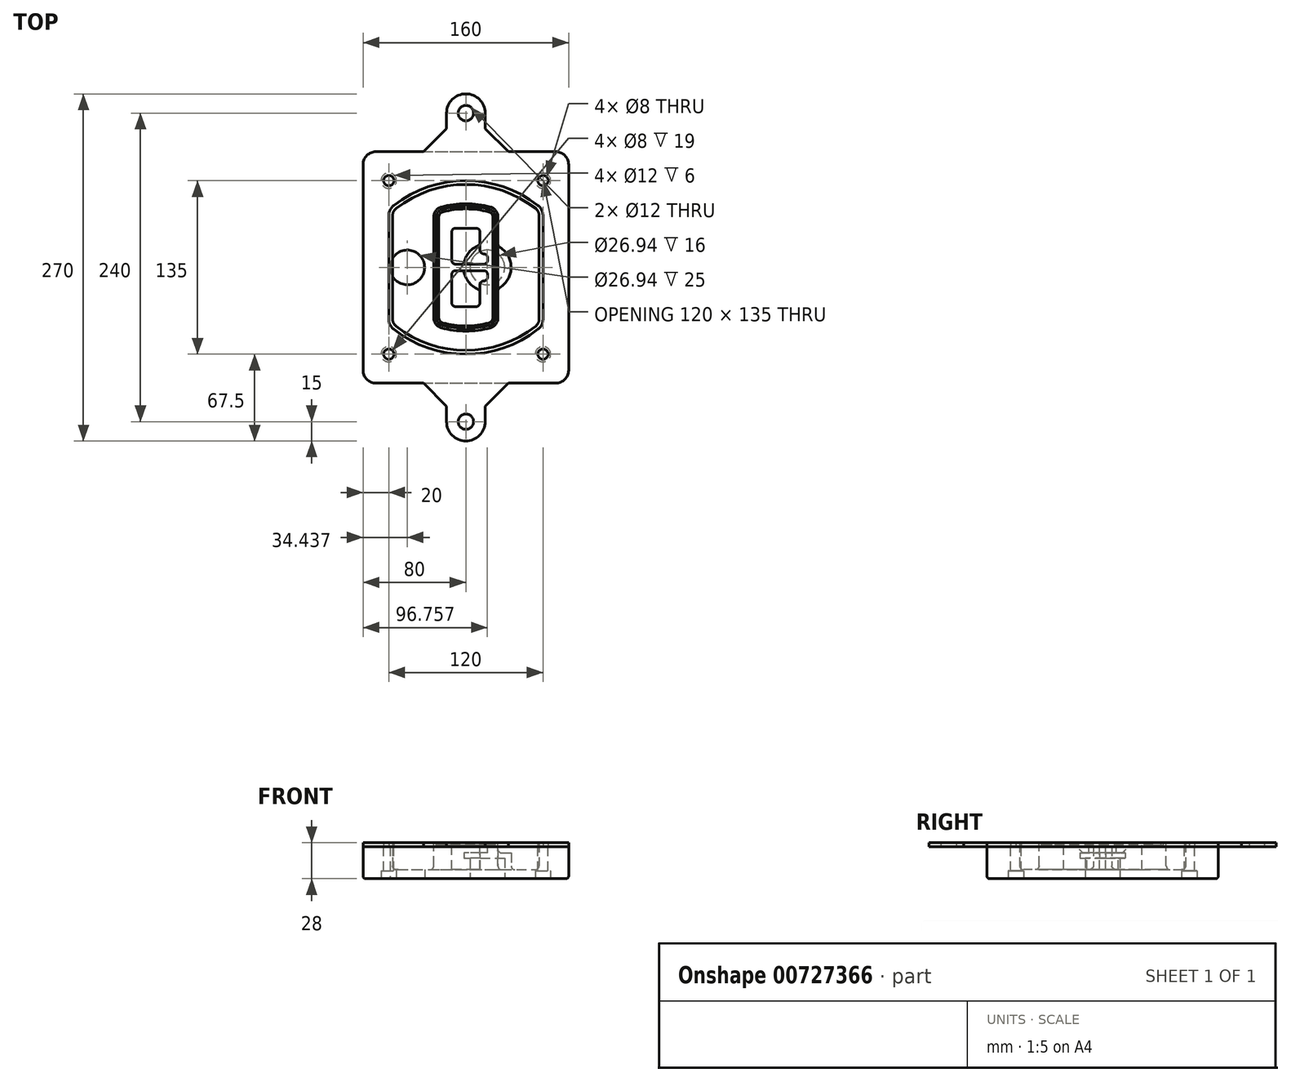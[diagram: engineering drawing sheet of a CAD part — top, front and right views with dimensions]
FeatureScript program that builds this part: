
annotation { "Feature Type Name" : "Feature", "Feature Type Description" : "" }
export const myFeature = defineFeature(function(context is Context, id is Id, definition is map)
    precondition{}
    {
        {
            var Q0;
            Q0=qCreatedBy(makeId("Top.planeOp"),FACE);
            var sketch = newSketch(context, id + "F0", { "sketchPlane" : qUnion([Q0])});
            skPoint(sketch, "E0.rect.middle", {"position": v(0, 0) * mm});
            skLineSegment(sketch, "E1.bottom", {"start": v(-70, -90) * mm, "end": v(70, -90) * mm});
            skLineSegment(sketch, "E1.top", {"start": v(-70, 90) * mm, "end": v(70, 90) * mm});
            skLineSegment(sketch, "E1.left", {"start": v(-80, -80) * mm, "end": v(-80, 80) * mm});
            skLineSegment(sketch, "E1.right", {"start": v(80, -80) * mm, "end": v(80, 80) * mm});
            skLineSegment(sketch, "E2", {"start": v(-80, 90) * mm, "end": v(80, -90) * mm, "construction": true});
            skLineSegment(sketch, "E3", {"start": v(80, 90) * mm, "end": v(-80, -90) * mm, "construction": true});
            skCircle(sketch, "E4", {"center": v(-60, 67.5) * mm, "radius": 4 * mm});
            skCircle(sketch, "E5", {"center": v(60, 67.5) * mm, "radius": 4 * mm});
            skCircle(sketch, "E6", {"center": v(60, -67.5) * mm, "radius": 4 * mm});
            skCircle(sketch, "E7", {"center": v(-60, -67.5) * mm, "radius": 4 * mm});
            skLineSegment(sketch, "E8", {"start": v(-60, 67.5) * mm, "end": v(60, 67.5) * mm, "construction": true});
            skLineSegment(sketch, "E9", {"start": v(60, 67.5) * mm, "end": v(60, -67.5) * mm, "construction": true});
            skLineSegment(sketch, "E10", {"start": v(60, -67.5) * mm, "end": v(-60, -67.5) * mm, "construction": true});
            skLineSegment(sketch, "E11", {"start": v(-60, -67.5) * mm, "end": v(-60, 67.5) * mm, "construction": true});
            skLineSegment(sketch, "E12", {"start": v(-60, 40.3) * mm, "end": v(-60, -40.3) * mm});
            skLineSegment(sketch, "E13", {"start": v(60, 40.3) * mm, "end": v(60, -40.3) * mm});
            skArc(sketch, "E14", {"start": v(56.15, 48.18) * mm, "mid": v(0, 67.5) * mm, "end": v(-56.15, 48.18) * mm});
            skArc(sketch, "E15", {"start": v(-56.15, -48.18) * mm, "mid": v(0, -67.5) * mm, "end": v(56.15, -48.18) * mm});
            skLineSegment(sketch, "E16", {"start": v(-60, 0) * mm, "end": v(60, 0) * mm, "construction": true});
            skPoint(sketch, "E17.visualSharp", {"position": v(-60, -45) * mm});
            skArc(sketch, "E17.filletArc", {"start": v(-60, -40.3) * mm, "mid": v(-58.99, -44.68) * mm, "end": v(-56.15, -48.18) * mm});
            skPoint(sketch, "E18.visualSharp", {"position": v(-60, 45) * mm});
            skArc(sketch, "E18.filletArc", {"start": v(-56.15, 48.18) * mm, "mid": v(-58.99, 44.68) * mm, "end": v(-60, 40.3) * mm});
            skPoint(sketch, "E19.visualSharp", {"position": v(60, 45) * mm});
            skArc(sketch, "E19.filletArc", {"start": v(60, 40.3) * mm, "mid": v(58.99, 44.68) * mm, "end": v(56.15, 48.18) * mm});
            skPoint(sketch, "E20.visualSharp", {"position": v(60, -45) * mm});
            skArc(sketch, "E20.filletArc", {"start": v(56.15, -48.18) * mm, "mid": v(58.99, -44.68) * mm, "end": v(60, -40.3) * mm});
            skPoint(sketch, "E21.visualSharp", {"position": v(-80, 90) * mm});
            skArc(sketch, "E21.filletArc", {"start": v(-70, 90) * mm, "mid": v(-77.07, 87.07) * mm, "end": v(-80, 80) * mm});
            skPoint(sketch, "E22.visualSharp", {"position": v(80, 90) * mm});
            skArc(sketch, "E22.filletArc", {"start": v(80, 80) * mm, "mid": v(77.07, 87.07) * mm, "end": v(70, 90) * mm});
            skPoint(sketch, "E23.visualSharp", {"position": v(80, -90) * mm});
            skArc(sketch, "E23.filletArc", {"start": v(70, -90) * mm, "mid": v(77.07, -87.07) * mm, "end": v(80, -80) * mm});
            skPoint(sketch, "E24.visualSharp", {"position": v(-80, -90) * mm});
            skArc(sketch, "E24.filletArc", {"start": v(-80, -80) * mm, "mid": v(-77.07, -87.07) * mm, "end": v(-70, -90) * mm});
            skArc(sketch, "E25.0", {"start": v(57, 40.3) * mm, "mid": v(56.3, 43.36) * mm, "end": v(54.3, 45.81) * mm});
            skLineSegment(sketch, "E25.1", {"start": v(57, 40.3) * mm, "end": v(57, -40.3) * mm});
            skArc(sketch, "E25.2", {"start": v(54.3, -45.81) * mm, "mid": v(56.3, -43.36) * mm, "end": v(57, -40.3) * mm});
            skArc(sketch, "E25.3", {"start": v(-54.3, -45.81) * mm, "mid": v(0, -64.5) * mm, "end": v(54.3, -45.81) * mm});
            skArc(sketch, "E25.4", {"start": v(-57, -40.3) * mm, "mid": v(-56.3, -43.36) * mm, "end": v(-54.3, -45.81) * mm});
            skArc(sketch, "E25.5", {"start": v(54.3, 45.81) * mm, "mid": v(0, 64.5) * mm, "end": v(-54.3, 45.81) * mm});
            skLineSegment(sketch, "E25.6", {"start": v(-57, 40.3) * mm, "end": v(-57, -40.3) * mm});
            skArc(sketch, "E25.7", {"start": v(-54.3, 45.81) * mm, "mid": v(-56.3, 43.36) * mm, "end": v(-57, 40.3) * mm});
            skArc(sketch, "E26.0", {"start": v(-58.62, 51.33) * mm, "mid": v(-62.58, 46.43) * mm, "end": v(-64, 40.3) * mm});
            skArc(sketch, "E26.1", {"start": v(58.62, 51.33) * mm, "mid": v(0, 71.5) * mm, "end": v(-58.62, 51.33) * mm});
            skArc(sketch, "E26.2", {"start": v(64, 40.3) * mm, "mid": v(62.58, 46.43) * mm, "end": v(58.62, 51.33) * mm});
            skLineSegment(sketch, "E26.3", {"start": v(64, 40.3) * mm, "end": v(64, -40.3) * mm});
            skArc(sketch, "E26.4", {"start": v(58.62, -51.33) * mm, "mid": v(62.58, -46.43) * mm, "end": v(64, -40.3) * mm});
            skLineSegment(sketch, "E26.5", {"start": v(-64, 40.3) * mm, "end": v(-64, -40.3) * mm});
            skArc(sketch, "E26.6", {"start": v(-58.62, -51.33) * mm, "mid": v(0, -71.5) * mm, "end": v(58.62, -51.33) * mm});
            skArc(sketch, "E26.7", {"start": v(-64, -40.3) * mm, "mid": v(-62.58, -46.43) * mm, "end": v(-58.62, -51.33) * mm});
            skSolve(sketch);
        }
        {
            var Q0;
            Q0=makeQuery(id+"F0.imprint","IMPRINT",FACE,{"disambiguationData":[TD([[makeQuery(id+"F0.imprint","IMPRINT",EDGE,{"derivedFrom":sQuery(id+"F0.wireOp",EDGE,"E1.bottom")}),1.0]])]});
            var Q1;
            Q1=makeQuery(id+"F0.imprint","IMPRINT",FACE,{"disambiguationData":[TD([[makeQuery(id+"F0.imprint","IMPRINT",EDGE,{"derivedFrom":sQuery(id+"F0.wireOp",EDGE,"E12")}),1.0]])]});
            var Q2;
            Q2=makeQuery(id+"F0.imprint","IMPRINT",FACE,{"disambiguationData":[TD([[makeQuery(id+"F0.imprint","IMPRINT",EDGE,{"derivedFrom":sQuery(id+"F0.wireOp",EDGE,"E25.0")}),1.0]])]});
            var Q3;
            Q3=makeQuery(id+"F0.imprint","IMPRINT",FACE,{"disambiguationData":[TD([[makeQuery(id+"F0.imprint","IMPRINT",EDGE,{"derivedFrom":sQuery(id+"F0.wireOp",EDGE,"E12")}),-1.0]])]});
            extrude(context, id + "F1", {"entities" : qUnion([Q0, Q1, Q2, Q3]), "oppositeDirection" : true, "depth" : 25 * mm});
        }
        {
            var Q0;
            Q0=makeQuery(id+"F0.imprint","IMPRINT",FACE,{"disambiguationData":[TD([[makeQuery(id+"F0.imprint","IMPRINT",EDGE,{"derivedFrom":sQuery(id+"F0.wireOp",EDGE,"E12")}),1.0]])]});
            extrude(context, id + "F2", {"entities" : qUnion([Q0]), "operationType" : NewBodyOperationType.ADD, "depth" : 3 * mm});
        }
        {
            var Q0;
            Q0=makeQuery(id+"F0.imprint","IMPRINT",FACE,{"disambiguationData":[TD([[makeQuery(id+"F0.imprint","IMPRINT",EDGE,{"derivedFrom":sQuery(id+"F0.wireOp",EDGE,"E25.0")}),1.0]])]});
            extrude(context, id + "F3", {"entities" : qUnion([Q0]), "operationType" : NewBodyOperationType.REMOVE, "oppositeDirection" : true, "depth" : 18 * mm});
        }
        {
            var Q0;
            Q0=makeQuery(id+"F2.opExtrude","CAP_FACE",FACE,{"disambiguationData":[OSD([sQuery(id+"F0.wireOp",EDGE,"E12"),sQuery(id+"F0.wireOp",EDGE,"E13"),sQuery(id+"F0.wireOp",EDGE,"E14"),sQuery(id+"F0.wireOp",EDGE,"E15"),sQuery(id+"F0.wireOp",EDGE,"E17.filletArc"),sQuery(id+"F0.wireOp",EDGE,"E18.filletArc"),sQuery(id+"F0.wireOp",EDGE,"E19.filletArc"),sQuery(id+"F0.wireOp",EDGE,"E20.filletArc"),sQuery(id+"F0.wireOp",EDGE,"E25.0"),sQuery(id+"F0.wireOp",EDGE,"E25.1"),sQuery(id+"F0.wireOp",EDGE,"E25.2"),sQuery(id+"F0.wireOp",EDGE,"E25.3"),sQuery(id+"F0.wireOp",EDGE,"E25.4"),sQuery(id+"F0.wireOp",EDGE,"E25.5"),sQuery(id+"F0.wireOp",EDGE,"E25.6"),sQuery(id+"F0.wireOp",EDGE,"E25.7")])],"isStart":false});
            var sketch = newSketch(context, id + "F4", { "sketchPlane" : qUnion([Q0])});
            skArc(sketch, "E27.0", {"start": v(-19.08, -46.97) * mm, "mid": v(0, -49.5) * mm, "end": v(19.08, -46.97) * mm});
            skArc(sketch, "E28.0", {"start": v(19.08, 46.97) * mm, "mid": v(0, 49.5) * mm, "end": v(-19.08, 46.97) * mm});
            skLineSegment(sketch, "E29", {"start": v(-25, 39.25) * mm, "end": v(-25, -39.25) * mm});
            skLineSegment(sketch, "E30", {"start": v(25, 39.25) * mm, "end": v(25, -39.25) * mm});
            skLineSegment(sketch, "E31", {"start": v(-25, 45.1) * mm, "end": v(25, 45.1) * mm, "construction": true});
            skLineSegment(sketch, "E32", {"start": v(-25, -45.1) * mm, "end": v(25, -45.1) * mm, "construction": true});
            skPoint(sketch, "E33.visualSharp", {"position": v(-25, 45.1) * mm});
            skArc(sketch, "E33.filletArc", {"start": v(-19.08, 46.97) * mm, "mid": v(-23.35, 44.11) * mm, "end": v(-25, 39.25) * mm});
            skPoint(sketch, "E34.visualSharp", {"position": v(25, 45.1) * mm});
            skArc(sketch, "E34.filletArc", {"start": v(25, 39.25) * mm, "mid": v(23.35, 44.11) * mm, "end": v(19.08, 46.97) * mm});
            skPoint(sketch, "E35.visualSharp", {"position": v(25, -45.1) * mm});
            skArc(sketch, "E35.filletArc", {"start": v(19.08, -46.97) * mm, "mid": v(23.35, -44.11) * mm, "end": v(25, -39.25) * mm});
            skPoint(sketch, "E36.visualSharp", {"position": v(-25, -45.1) * mm});
            skArc(sketch, "E36.filletArc", {"start": v(-25, -39.25) * mm, "mid": v(-23.35, -44.11) * mm, "end": v(-19.08, -46.97) * mm});
            skArc(sketch, "E37.0", {"start": v(54.3, 45.81) * mm, "mid": v(0, 64.5) * mm, "end": v(-54.3, 45.81) * mm});
            skArc(sketch, "E37.1", {"start": v(-54.3, 45.81) * mm, "mid": v(-56.3, 43.36) * mm, "end": v(-57, 40.3) * mm});
            skLineSegment(sketch, "E37.2", {"start": v(-57, 40.3) * mm, "end": v(-57, -40.3) * mm});
            skArc(sketch, "E37.3", {"start": v(-57, -40.3) * mm, "mid": v(-56.3, -43.36) * mm, "end": v(-54.3, -45.81) * mm});
            skArc(sketch, "E37.4", {"start": v(-54.3, -45.81) * mm, "mid": v(0, -64.5) * mm, "end": v(54.3, -45.81) * mm});
            skArc(sketch, "E37.5", {"start": v(54.3, -45.81) * mm, "mid": v(56.3, -43.36) * mm, "end": v(57, -40.3) * mm});
            skLineSegment(sketch, "E37.6", {"start": v(57, 40.3) * mm, "end": v(57, -40.3) * mm});
            skArc(sketch, "E37.7", {"start": v(57, 40.3) * mm, "mid": v(56.3, 43.36) * mm, "end": v(54.3, 45.81) * mm});
            skLineSegment(sketch, "E38.0", {"start": v(23, 39.25) * mm, "end": v(23, -39.25) * mm});
            skArc(sketch, "E38.1", {"start": v(18.56, -45.04) * mm, "mid": v(21.76, -42.9) * mm, "end": v(23, -39.25) * mm});
            skArc(sketch, "E38.2", {"start": v(-18.56, -45.04) * mm, "mid": v(0, -47.5) * mm, "end": v(18.56, -45.04) * mm});
            skArc(sketch, "E38.3", {"start": v(-23, -39.25) * mm, "mid": v(-21.76, -42.9) * mm, "end": v(-18.56, -45.04) * mm});
            skLineSegment(sketch, "E38.4", {"start": v(-23, 39.25) * mm, "end": v(-23, -39.25) * mm});
            skArc(sketch, "E38.5", {"start": v(23, 39.25) * mm, "mid": v(21.76, 42.9) * mm, "end": v(18.56, 45.04) * mm});
            skArc(sketch, "E38.6", {"start": v(-18.56, 45.04) * mm, "mid": v(-21.76, 42.9) * mm, "end": v(-23, 39.25) * mm});
            skArc(sketch, "E38.7", {"start": v(18.56, 45.04) * mm, "mid": v(0, 47.5) * mm, "end": v(-18.56, 45.04) * mm});
            skArc(sketch, "E39.0", {"start": v(21, 39.25) * mm, "mid": v(20.18, 41.68) * mm, "end": v(18.04, 43.1) * mm});
            skLineSegment(sketch, "E39.1", {"start": v(21, 39.25) * mm, "end": v(21, -39.25) * mm});
            skArc(sketch, "E39.2", {"start": v(18.04, -43.1) * mm, "mid": v(20.18, -41.68) * mm, "end": v(21, -39.25) * mm});
            skArc(sketch, "E39.3", {"start": v(-18.04, -43.1) * mm, "mid": v(0, -45.5) * mm, "end": v(18.04, -43.1) * mm});
            skArc(sketch, "E39.4", {"start": v(-21, -39.25) * mm, "mid": v(-20.18, -41.68) * mm, "end": v(-18.04, -43.1) * mm});
            skArc(sketch, "E39.5", {"start": v(18.04, 43.1) * mm, "mid": v(0, 45.5) * mm, "end": v(-18.04, 43.1) * mm});
            skLineSegment(sketch, "E39.6", {"start": v(-21, 39.25) * mm, "end": v(-21, -39.25) * mm});
            skArc(sketch, "E39.7", {"start": v(-18.04, 43.1) * mm, "mid": v(-20.18, 41.68) * mm, "end": v(-21, 39.25) * mm});
            skLineSegment(sketch, "E40", {"start": v(-25, 0) * mm, "end": v(25, 0) * mm, "construction": true});
            skLineSegment(sketch, "E41", {"start": v(-11, 5.5) * mm, "end": v(-11, 27.5) * mm});
            skLineSegment(sketch, "E42", {"start": v(-8, 30.5) * mm, "end": v(8, 30.5) * mm});
            skLineSegment(sketch, "E43", {"start": v(11, 27.5) * mm, "end": v(11, 13.5) * mm});
            skLineSegment(sketch, "E44", {"start": v(14, 10.5) * mm, "end": v(14, 10.5) * mm});
            skLineSegment(sketch, "E45", {"start": v(17, 7.5) * mm, "end": v(17, 5.5) * mm});
            skLineSegment(sketch, "E46", {"start": v(14, 2.5) * mm, "end": v(-8, 2.5) * mm});
            skPoint(sketch, "E47.visualSharp", {"position": v(-11, 30.5) * mm});
            skArc(sketch, "E47.filletArc", {"start": v(-8, 30.5) * mm, "mid": v(-10.12, 29.62) * mm, "end": v(-11, 27.5) * mm});
            skPoint(sketch, "E48.visualSharp", {"position": v(11, 30.5) * mm});
            skArc(sketch, "E48.filletArc", {"start": v(11, 27.5) * mm, "mid": v(10.12, 29.62) * mm, "end": v(8, 30.5) * mm});
            skPoint(sketch, "E49.visualSharp", {"position": v(11, 10.5) * mm});
            skArc(sketch, "E49.filletArc", {"start": v(11, 13.5) * mm, "mid": v(11.88, 11.38) * mm, "end": v(14, 10.5) * mm});
            skPoint(sketch, "E50.visualSharp", {"position": v(17, 10.5) * mm});
            skArc(sketch, "E50.filletArc", {"start": v(17, 7.5) * mm, "mid": v(16.12, 9.62) * mm, "end": v(14, 10.5) * mm});
            skPoint(sketch, "E51.visualSharp", {"position": v(17, 2.5) * mm});
            skArc(sketch, "E51.filletArc", {"start": v(14, 2.5) * mm, "mid": v(16.12, 3.38) * mm, "end": v(17, 5.5) * mm});
            skPoint(sketch, "E52.visualSharp", {"position": v(-11, 2.5) * mm});
            skArc(sketch, "E52.filletArc", {"start": v(-11, 5.5) * mm, "mid": v(-10.12, 3.38) * mm, "end": v(-8, 2.5) * mm});
            skLineSegment(sketch, "E53.0.MirrorCS", {"start": v(14, -2.5) * mm, "end": v(-8, -2.5) * mm});
            skArc(sketch, "E54.0.MirrorCS", {"start": v(-11, -5.5) * mm, "mid": v(-10.12, -3.38) * mm, "end": v(-8, -2.5) * mm});
            skLineSegment(sketch, "E55.0.MirrorCS", {"start": v(-11, -5.5) * mm, "end": v(-11, -27.5) * mm});
            skArc(sketch, "E56.0.MirrorCS", {"start": v(-8, -30.5) * mm, "mid": v(-10.12, -29.62) * mm, "end": v(-11, -27.5) * mm});
            skLineSegment(sketch, "E57.0.MirrorCS", {"start": v(-8, -30.5) * mm, "end": v(8, -30.5) * mm});
            skArc(sketch, "E58.0.MirrorCS", {"start": v(11, -27.5) * mm, "mid": v(10.12, -29.62) * mm, "end": v(8, -30.5) * mm});
            skLineSegment(sketch, "E59.0.MirrorCS", {"start": v(11, -27.5) * mm, "end": v(11, -13.5) * mm});
            skArc(sketch, "E60.0.MirrorCS", {"start": v(11, -13.5) * mm, "mid": v(11.88, -11.38) * mm, "end": v(14, -10.5) * mm});
            skArc(sketch, "E61.0.MirrorCS", {"start": v(17, -7.5) * mm, "mid": v(16.12, -9.62) * mm, "end": v(14, -10.5) * mm});
            skLineSegment(sketch, "E62.0.MirrorCS", {"start": v(17, -7.5) * mm, "end": v(17, -5.5) * mm});
            skArc(sketch, "E63.0.MirrorCS", {"start": v(14, -2.5) * mm, "mid": v(16.12, -3.38) * mm, "end": v(17, -5.5) * mm});
            skSolve(sketch);
        }
        {
            var Q0;
            Q0=makeQuery(id+"F4.imprint","IMPRINT",FACE,{"disambiguationData":[TD([[makeQuery(id+"F4.imprint","IMPRINT",EDGE,{"derivedFrom":sQuery(id+"F4.wireOp",EDGE,"E27.0")}),1.0]])]});
            var Q1;
            Q1=makeQuery(id+"F4.imprint","IMPRINT",FACE,{"disambiguationData":[TD([[makeQuery(id+"F4.imprint","IMPRINT",EDGE,{"derivedFrom":sQuery(id+"F4.wireOp",EDGE,"E38.0")}),-1.0]])]});
            var Q2;
            Q2=makeQuery(id+"F4.imprint","IMPRINT",FACE,{"disambiguationData":[TD([[makeQuery(id+"F4.imprint","IMPRINT",EDGE,{"derivedFrom":sQuery(id+"F4.wireOp",EDGE,"E39.0")}),1.0]])]});
            extrude(context, id + "F5", {"entities" : qUnion([Q0, Q1, Q2]), "operationType" : NewBodyOperationType.ADD, "endBound" : BoundingType.UP_TO_NEXT, "oppositeDirection" : true, "depth" : 25 * mm});
        }
        {
            var Q0;
            Q0=makeQuery(id+"F4.imprint","IMPRINT",FACE,{"disambiguationData":[TD([[makeQuery(id+"F4.imprint","IMPRINT",EDGE,{"derivedFrom":sQuery(id+"F4.wireOp",EDGE,"E38.0")}),-1.0]])]});
            extrude(context, id + "F6", {"entities" : qUnion([Q0]), "operationType" : NewBodyOperationType.REMOVE, "oppositeDirection" : true, "depth" : 2 * mm});
        }
        {
            var Q0;
            Q0=makeQuery(id+"F1.opExtrude","CAP_FACE",FACE,{"disambiguationData":[OSD([sQuery(id+"F0.wireOp",EDGE,"E1.bottom"),sQuery(id+"F0.wireOp",EDGE,"E1.top"),sQuery(id+"F0.wireOp",EDGE,"E1.left"),sQuery(id+"F0.wireOp",EDGE,"E1.right"),sQuery(id+"F0.wireOp",EDGE,"E4"),sQuery(id+"F0.wireOp",EDGE,"E5"),sQuery(id+"F0.wireOp",EDGE,"E6"),sQuery(id+"F0.wireOp",EDGE,"E7"),sQuery(id+"F0.wireOp",EDGE,"E21.filletArc"),sQuery(id+"F0.wireOp",EDGE,"E22.filletArc"),sQuery(id+"F0.wireOp",EDGE,"E23.filletArc"),sQuery(id+"F0.wireOp",EDGE,"E24.filletArc")])],"isStart":false});
            var sketch = newSketch(context, id + "F7", { "sketchPlane" : qUnion([Q0])});
            skCircle(sketch, "E64", {"center": v(16.76, 0) * mm, "radius": 13.47 * mm});
            skCircle(sketch, "E65", {"center": v(-45.56, 0) * mm, "radius": 13.47 * mm});
            skLineSegment(sketch, "E66", {"start": v(80, 0) * mm, "end": v(-80, 0) * mm});
            skCircle(sketch, "E67", {"center": v(16.76, 0) * mm, "radius": 18.47 * mm});
            skCircle(sketch, "E68", {"center": v(60, -67.5) * mm, "radius": 6 * mm});
            skCircle(sketch, "E69", {"center": v(-60, -67.5) * mm, "radius": 6 * mm});
            skCircle(sketch, "E70", {"center": v(-60, 67.5) * mm, "radius": 6 * mm});
            skCircle(sketch, "E71", {"center": v(60, 67.5) * mm, "radius": 6 * mm});
            skSolve(sketch);
        }
        {
            var Q0;
            {var subQ1=sQuery(id+"F7.wireOp",EDGE,"E66");var subQ4=sQuery(id+"F7.wireOp",EDGE,"E64");var subQ6=makeQuery(id+"F7.imprint","INTERSECT",VERTEX,{"disambiguationData":[OD(0.0)],"derivedFrom":[subQ4,subQ1]});Q0=makeQuery(id+"F7.imprint","IMPRINT",FACE,{"disambiguationData":[TD([[makeQuery(id+"F7.imprint","IMPRINT",EDGE,{"disambiguationData":[TD([[subQ6,-1.0]])],"derivedFrom":subQ4}),-1.0]])]});}
            var Q1;
            {var subQ0=sQuery(id+"F7.wireOp",EDGE,"E66");var subQ1=sQuery(id+"F7.wireOp",EDGE,"E64");var subQ3=makeQuery(id+"F7.imprint","INTERSECT",VERTEX,{"disambiguationData":[OD(0.0)],"derivedFrom":[subQ1,subQ0]});Q1=makeQuery(id+"F7.imprint","IMPRINT",FACE,{"disambiguationData":[TD([[makeQuery(id+"F7.imprint","IMPRINT",EDGE,{"disambiguationData":[TD([[subQ3,-1.0]])],"derivedFrom":subQ1}),1.0]])]});}
            var Q2;
            {var subQ0=sQuery(id+"F7.wireOp",EDGE,"E66");var subQ1=sQuery(id+"F7.wireOp",EDGE,"E64");var subQ3=makeQuery(id+"F7.imprint","INTERSECT",VERTEX,{"disambiguationData":[OD(0.0)],"derivedFrom":[subQ1,subQ0]});Q2=makeQuery(id+"F7.imprint","IMPRINT",FACE,{"disambiguationData":[TD([[makeQuery(id+"F7.imprint","IMPRINT",EDGE,{"disambiguationData":[TD([[subQ3,1.0]])],"derivedFrom":subQ1}),1.0]])]});}
            var Q3;
            {var subQ1=sQuery(id+"F7.wireOp",EDGE,"E66");var subQ4=sQuery(id+"F7.wireOp",EDGE,"E64");var subQ6=makeQuery(id+"F7.imprint","INTERSECT",VERTEX,{"disambiguationData":[OD(0.0)],"derivedFrom":[subQ4,subQ1]});Q3=makeQuery(id+"F7.imprint","IMPRINT",FACE,{"disambiguationData":[TD([[makeQuery(id+"F7.imprint","IMPRINT",EDGE,{"disambiguationData":[TD([[subQ6,1.0]])],"derivedFrom":subQ4}),-1.0]])]});}
            extrude(context, id + "F8", {"entities" : qUnion([Q0, Q1, Q2, Q3]), "operationType" : NewBodyOperationType.ADD, "oppositeDirection" : true, "depth" : 20 * mm});
        }
        {
            var Q0;
            {var subQ0=sQuery(id+"F7.wireOp",EDGE,"E66");var subQ1=sQuery(id+"F7.wireOp",EDGE,"E64");var subQ3=makeQuery(id+"F7.imprint","INTERSECT",VERTEX,{"disambiguationData":[OD(0.0)],"derivedFrom":[subQ1,subQ0]});Q0=makeQuery(id+"F7.imprint","IMPRINT",FACE,{"disambiguationData":[TD([[makeQuery(id+"F7.imprint","IMPRINT",EDGE,{"disambiguationData":[TD([[subQ3,-1.0]])],"derivedFrom":subQ1}),1.0]])]});}
            var Q1;
            {var subQ0=sQuery(id+"F7.wireOp",EDGE,"E66");var subQ1=sQuery(id+"F7.wireOp",EDGE,"E64");var subQ3=makeQuery(id+"F7.imprint","INTERSECT",VERTEX,{"disambiguationData":[OD(0.0)],"derivedFrom":[subQ1,subQ0]});Q1=makeQuery(id+"F7.imprint","IMPRINT",FACE,{"disambiguationData":[TD([[makeQuery(id+"F7.imprint","IMPRINT",EDGE,{"disambiguationData":[TD([[subQ3,1.0]])],"derivedFrom":subQ1}),1.0]])]});}
            extrude(context, id + "F9", {"entities" : qUnion([Q0, Q1]), "operationType" : NewBodyOperationType.REMOVE, "oppositeDirection" : true, "depth" : 16 * mm});
        }
        {
            var Q0;
            {var subQ0=sQuery(id+"F7.wireOp",EDGE,"E66");var subQ1=sQuery(id+"F7.wireOp",EDGE,"E65");var subQ3=makeQuery(id+"F7.imprint","INTERSECT",VERTEX,{"disambiguationData":[OD(0.0)],"derivedFrom":[subQ1,subQ0]});Q0=makeQuery(id+"F7.imprint","IMPRINT",FACE,{"disambiguationData":[TD([[makeQuery(id+"F7.imprint","IMPRINT",EDGE,{"disambiguationData":[TD([[subQ3,-1.0]])],"derivedFrom":subQ1}),1.0]])]});}
            var Q1;
            {var subQ0=sQuery(id+"F7.wireOp",EDGE,"E66");var subQ1=sQuery(id+"F7.wireOp",EDGE,"E65");var subQ3=makeQuery(id+"F7.imprint","INTERSECT",VERTEX,{"disambiguationData":[OD(0.0)],"derivedFrom":[subQ1,subQ0]});Q1=makeQuery(id+"F7.imprint","IMPRINT",FACE,{"disambiguationData":[TD([[makeQuery(id+"F7.imprint","IMPRINT",EDGE,{"disambiguationData":[TD([[subQ3,1.0]])],"derivedFrom":subQ1}),1.0]])]});}
            extrude(context, id + "F10", {"entities" : qUnion([Q0, Q1]), "operationType" : NewBodyOperationType.REMOVE, "oppositeDirection" : true, "depth" : 25 * mm});
        }
        {
            var Q0;
            Q0=makeQuery(id+"F7.imprint","IMPRINT",FACE,{"disambiguationData":[TD([[makeQuery(id+"F7.imprint","IMPRINT",EDGE,{"derivedFrom":sQuery(id+"F7.wireOp",EDGE,"E68")}),1.0]])]});
            var Q1;
            Q1=makeQuery(id+"F7.imprint","IMPRINT",FACE,{"disambiguationData":[TD([[makeQuery(id+"F7.imprint","IMPRINT",EDGE,{"derivedFrom":makeQuery(id+"F1.opExtrude","CAP_EDGE",EDGE,{"disambiguationData":[OSD([sQuery(id+"F0.wireOp",EDGE,"E5")])],"isStart":false})}),-1.0]])]});
            var Q2;
            Q2=makeQuery(id+"F7.imprint","IMPRINT",FACE,{"disambiguationData":[TD([[makeQuery(id+"F7.imprint","IMPRINT",EDGE,{"derivedFrom":sQuery(id+"F7.wireOp",EDGE,"E69")}),1.0]])]});
            var Q3;
            Q3=makeQuery(id+"F7.imprint","IMPRINT",FACE,{"disambiguationData":[TD([[makeQuery(id+"F7.imprint","IMPRINT",EDGE,{"derivedFrom":makeQuery(id+"F1.opExtrude","CAP_EDGE",EDGE,{"disambiguationData":[OSD([sQuery(id+"F0.wireOp",EDGE,"E4")])],"isStart":false})}),-1.0]])]});
            var Q4;
            Q4=makeQuery(id+"F7.imprint","IMPRINT",FACE,{"disambiguationData":[TD([[makeQuery(id+"F7.imprint","IMPRINT",EDGE,{"derivedFrom":sQuery(id+"F7.wireOp",EDGE,"E70")}),1.0]])]});
            var Q5;
            Q5=makeQuery(id+"F7.imprint","IMPRINT",FACE,{"disambiguationData":[TD([[makeQuery(id+"F7.imprint","IMPRINT",EDGE,{"derivedFrom":makeQuery(id+"F1.opExtrude","CAP_EDGE",EDGE,{"disambiguationData":[OSD([sQuery(id+"F0.wireOp",EDGE,"E7")])],"isStart":false})}),-1.0]])]});
            var Q6;
            Q6=makeQuery(id+"F7.imprint","IMPRINT",FACE,{"disambiguationData":[TD([[makeQuery(id+"F7.imprint","IMPRINT",EDGE,{"derivedFrom":sQuery(id+"F7.wireOp",EDGE,"E71")}),1.0]])]});
            var Q7;
            Q7=makeQuery(id+"F7.imprint","IMPRINT",FACE,{"disambiguationData":[TD([[makeQuery(id+"F7.imprint","IMPRINT",EDGE,{"derivedFrom":makeQuery(id+"F1.opExtrude","CAP_EDGE",EDGE,{"disambiguationData":[OSD([sQuery(id+"F0.wireOp",EDGE,"E6")])],"isStart":false})}),-1.0]])]});
            extrude(context, id + "F11", {"entities" : qUnion([Q0, Q1, Q2, Q3, Q4, Q5, Q6, Q7]), "operationType" : NewBodyOperationType.REMOVE, "oppositeDirection" : true, "depth" : 6 * mm});
        }
        {
            var Q0;
            Q0=makeQuery(id+"F9.boolean.opBoolean","COPY",FACE,{"derivedFrom":makeQuery(id+"F9.opExtrude","CAP_FACE",FACE,{"disambiguationData":[OSD([sQuery(id+"F7.wireOp",EDGE,"E64")])],"isStart":false})});
            var sketch = newSketch(context, id + "F12", { "sketchPlane" : qUnion([Q0])});
            skArc(sketch, "E72.0", {"start": v(11, 17.55) * mm, "mid": v(2.57, 11.82) * mm, "end": v(-1.54, 2.5) * mm});
            skArc(sketch, "E72.1", {"start": v(-1.54, -2.5) * mm, "mid": v(2.57, -11.82) * mm, "end": v(11, -17.55) * mm});
            skLineSegment(sketch, "E73", {"start": v(-1.54, -2.5) * mm, "end": v(14, -2.5) * mm});
            skLineSegment(sketch, "E74.0", {"start": v(14, 2.5) * mm, "end": v(-1.54, 2.5) * mm});
            skArc(sketch, "E74.1", {"start": v(14, 2.5) * mm, "mid": v(16.12, 3.38) * mm, "end": v(17, 5.5) * mm});
            skLineSegment(sketch, "E74.2", {"start": v(17, 7.5) * mm, "end": v(17, 5.5) * mm});
            skArc(sketch, "E74.3", {"start": v(17, 7.5) * mm, "mid": v(16.12, 9.62) * mm, "end": v(14, 10.5) * mm});
            skArc(sketch, "E74.4", {"start": v(11, 13.5) * mm, "mid": v(11.88, 11.38) * mm, "end": v(14, 10.5) * mm});
            skLineSegment(sketch, "E74.5", {"start": v(11, 17.55) * mm, "end": v(11, 13.5) * mm});
            skLineSegment(sketch, "E74.7", {"start": v(14, -2.5) * mm, "end": v(-1.54, -2.5) * mm});
            skArc(sketch, "E74.8", {"start": v(14, -2.5) * mm, "mid": v(16.12, -3.38) * mm, "end": v(17, -5.5) * mm});
            skLineSegment(sketch, "E74.9", {"start": v(17, -7.5) * mm, "end": v(17, -5.5) * mm});
            skArc(sketch, "E74.10", {"start": v(17, -7.5) * mm, "mid": v(16.12, -9.62) * mm, "end": v(14, -10.5) * mm});
            skArc(sketch, "E74.11", {"start": v(11, -13.5) * mm, "mid": v(11.88, -11.38) * mm, "end": v(14, -10.5) * mm});
            skLineSegment(sketch, "E74.12", {"start": v(11, -17.55) * mm, "end": v(11, -13.5) * mm});
            skPoint(sketch, "E75.orphan", {"position": v(11, -27.5) * mm});
            skPoint(sketch, "E76.orphan", {"position": v(-8, -2.5) * mm});
            skPoint(sketch, "E77.orphan", {"position": v(-8, 2.5) * mm});
            skPoint(sketch, "E78.orphan", {"position": v(11, 27.5) * mm});
            skSolve(sketch);
        }
        {
            var Q0;
            {var subQ7=sQuery(id+"F12.wireOp",EDGE,"E72.0");var subQ14=sQuery(id+"F12.wireOp",EDGE,"E72.1");var subQ16=sQuery(id+"F12.wireOp",EDGE,"E74.1");var subQ18=sQuery(id+"F12.wireOp",EDGE,"E74.8");Q0=qUnion([makeQuery(id+"F12.imprint","IMPRINT",FACE,{"disambiguationData":[TD([[makeQuery(id+"F12.imprint","IMPRINT",EDGE,{"derivedFrom":subQ7}),1.0]])]}),makeQuery(id+"F12.imprint","IMPRINT",FACE,{"disambiguationData":[TD([[makeQuery(id+"F12.imprint","IMPRINT",EDGE,{"derivedFrom":subQ14}),1.0]])]}),makeQuery(id+"F12.imprint","IMPRINT",FACE,{"disambiguationData":[TD([[makeQuery(id+"F12.imprint","IMPRINT",EDGE,{"derivedFrom":subQ16}),1.0]])]}),makeQuery(id+"F12.imprint","IMPRINT",FACE,{"disambiguationData":[TD([[makeQuery(id+"F12.imprint","IMPRINT",EDGE,{"derivedFrom":subQ18}),-1.0]])]})]);}
            var Q1;
            Q1=makeQuery(id+"F5.boolean.opBoolean","SPLIT",FACE,{"disambiguationData":[TD([makeQuery(id+"F5.opExtrude","SWEPT_FACE",FACE,{"disambiguationData":[OSD([sQuery(id+"F4.wireOp",EDGE,"E41")])]})])],"derivedFrom":makeQuery(id+"F3.boolean.opBoolean","COPY",FACE,{"derivedFrom":makeQuery(id+"F3.opExtrude","CAP_FACE",FACE,{"disambiguationData":[OSD([sQuery(id+"F0.wireOp",EDGE,"E25.0"),sQuery(id+"F0.wireOp",EDGE,"E25.1"),sQuery(id+"F0.wireOp",EDGE,"E25.2"),sQuery(id+"F0.wireOp",EDGE,"E25.3"),sQuery(id+"F0.wireOp",EDGE,"E25.4"),sQuery(id+"F0.wireOp",EDGE,"E25.5"),sQuery(id+"F0.wireOp",EDGE,"E25.6"),sQuery(id+"F0.wireOp",EDGE,"E25.7")])],"isStart":false})})});
            extrude(context, id + "F13", {"entities" : qUnion([Q0]), "operationType" : NewBodyOperationType.REMOVE, "endBound" : BoundingType.UP_TO_SURFACE, "endBoundEntityFace" : qUnion([Q1]), "depth" : 25 * mm});
        }
        {
            var Q0;
            Q0=makeQuery(id+"F3.boolean.opBoolean","COPY",EDGE,{"derivedFrom":makeQuery(id+"F3.opExtrude","CAP_EDGE",EDGE,{"disambiguationData":[OSD([sQuery(id+"F0.wireOp",EDGE,"E25.6")])],"isStart":false})});
            var Q1;
            Q1=makeQuery(id+"F8.boolean.opBoolean","INTERSECT",EDGE,{"derivedFrom":[makeQuery(id+"F5.opExtrude","SWEPT_FACE",FACE,{"disambiguationData":[OSD([sQuery(id+"F4.wireOp",EDGE,"E30")])]}),makeQuery(id+"F8.opExtrude","CAP_FACE",FACE,{"disambiguationData":[OSD([sQuery(id+"F7.wireOp",EDGE,"E67")])],"isStart":false})]});
            var Q2;
            Q2=makeQuery(id+"F8.boolean.opBoolean","INTERSECT",EDGE,{"disambiguationData":[OD(1.0)],"derivedFrom":[makeQuery(id+"F5.opExtrude","SWEPT_FACE",FACE,{"disambiguationData":[OSD([sQuery(id+"F4.wireOp",EDGE,"E30")])]}),makeQuery(id+"F8.opExtrude","SWEPT_FACE",FACE,{"disambiguationData":[OSD([sQuery(id+"F7.wireOp",EDGE,"E67")])]})]});
            var Q3;
            {var subQ0=sQuery(id+"F4.wireOp",EDGE,"E30");Q3=makeQuery(id+"F8.boolean.opBoolean","SPLIT",EDGE,{"disambiguationData":[TD([makeQuery(id+"F5.opExtrude","SWEPT_FACE",FACE,{"disambiguationData":[OSD([sQuery(id+"F4.wireOp",EDGE,"E35.filletArc")])]})])],"derivedFrom":makeQuery(id+"F5.opExtrude","CAP_EDGE",EDGE,{"disambiguationData":[OSD([subQ0])],"isStart":false})});}
            var Q4;
            {var subQ0=sQuery(id+"F0.wireOp",EDGE,"E25.7");var subQ1=sQuery(id+"F0.wireOp",EDGE,"E25.1");var subQ2=sQuery(id+"F0.wireOp",EDGE,"E25.6");var subQ3=sQuery(id+"F0.wireOp",EDGE,"E25.5");var subQ4=sQuery(id+"F0.wireOp",EDGE,"E25.4");var subQ5=sQuery(id+"F0.wireOp",EDGE,"E25.0");var subQ6=sQuery(id+"F0.wireOp",EDGE,"E25.2");var subQ7=sQuery(id+"F0.wireOp",EDGE,"E25.3");Q4=makeQuery(id+"F8.boolean.opBoolean","INTERSECT",EDGE,{"derivedFrom":[makeQuery(id+"F5.boolean.opBoolean","SPLIT",FACE,{"disambiguationData":[TD([makeQuery(id+"F2.opExtrude","SWEPT_FACE",FACE,{"disambiguationData":[OSD([subQ5])]})])],"derivedFrom":makeQuery(id+"F3.boolean.opBoolean","COPY",FACE,{"derivedFrom":makeQuery(id+"F3.opExtrude","CAP_FACE",FACE,{"disambiguationData":[OSD([subQ5,subQ1,subQ6,subQ7,subQ4,subQ3,subQ2,subQ0])],"isStart":false})})}),makeQuery(id+"F8.opExtrude","SWEPT_FACE",FACE,{"disambiguationData":[OSD([sQuery(id+"F7.wireOp",EDGE,"E67")])]})]});}
            var Q5;
            Q5=makeQuery(id+"F8.boolean.opBoolean","INTERSECT",EDGE,{"disambiguationData":[OD(0.0)],"derivedFrom":[makeQuery(id+"F5.opExtrude","SWEPT_FACE",FACE,{"disambiguationData":[OSD([sQuery(id+"F4.wireOp",EDGE,"E30")])]}),makeQuery(id+"F8.opExtrude","SWEPT_FACE",FACE,{"disambiguationData":[OSD([sQuery(id+"F7.wireOp",EDGE,"E67")])]})]});
            fillet(context, id + "F14", {"entities" : qUnion([Q0, Q1, Q2, Q3, Q4, Q5]), "radius" : 3 * mm, "tangentPropagation" : true, "allowEdgeOverflow" : false});
        }
        {
            var Q0;
            Q0=makeQuery(id+"F1.opExtrude","CAP_EDGE",EDGE,{"disambiguationData":[OSD([sQuery(id+"F0.wireOp",EDGE,"E1.bottom")])],"isStart":false});
            fillet(context, id + "F15", {"entities" : qUnion([Q0]), "radius" : 2 * mm, "tangentPropagation" : true, "allowEdgeOverflow" : false});
        }
        {
            var Q0;
            {var subQ0=sQuery(id+"F0.wireOp",EDGE,"E21.filletArc");var subQ1=sQuery(id+"F0.wireOp",EDGE,"E7");var subQ2=sQuery(id+"F0.wireOp",EDGE,"E6");var subQ3=sQuery(id+"F0.wireOp",EDGE,"E5");var subQ4=sQuery(id+"F0.wireOp",EDGE,"E4");var subQ5=sQuery(id+"F0.wireOp",EDGE,"E22.filletArc");var subQ6=sQuery(id+"F0.wireOp",EDGE,"E1.bottom");var subQ7=sQuery(id+"F0.wireOp",EDGE,"E1.right");var subQ8=sQuery(id+"F0.wireOp",EDGE,"E1.top");var subQ9=sQuery(id+"F0.wireOp",EDGE,"E1.left");var subQ10=sQuery(id+"F0.wireOp",EDGE,"E23.filletArc");var subQ11=sQuery(id+"F0.wireOp",EDGE,"E24.filletArc");Q0=makeQuery(id+"F2.boolean.opBoolean","SPLIT",FACE,{"disambiguationData":[TD([makeQuery(id+"F1.opExtrude","SWEPT_FACE",FACE,{"disambiguationData":[OSD([subQ6])]})])],"derivedFrom":makeQuery(id+"F1.opExtrude","CAP_FACE",FACE,{"disambiguationData":[OSD([subQ6,subQ8,subQ9,subQ7,subQ4,subQ3,subQ2,subQ1,subQ0,subQ5,subQ10,subQ11])],"isStart":true})});}
            var sketch = newSketch(context, id + "F16", { "sketchPlane" : qUnion([Q0])});
            skLineSegment(sketch, "E79.1", {"start": v(-80, -80) * mm, "end": v(-80, 80) * mm});
            skArc(sketch, "E79.2", {"start": v(-70, 90) * mm, "mid": v(-77.07, 87.07) * mm, "end": v(-80, 80) * mm});
            skLineSegment(sketch, "E79.3", {"start": v(-70, 90) * mm, "end": v(70, 90) * mm});
            skArc(sketch, "E79.4", {"start": v(80, 80) * mm, "mid": v(77.07, 87.07) * mm, "end": v(70, 90) * mm});
            skLineSegment(sketch, "E79.5", {"start": v(80, -80) * mm, "end": v(80, 80) * mm});
            skArc(sketch, "E79.6", {"start": v(70, -90) * mm, "mid": v(77.07, -87.07) * mm, "end": v(80, -80) * mm});
            skLineSegment(sketch, "E79.7", {"start": v(-70, -90) * mm, "end": v(70, -90) * mm});
            skArc(sketch, "E79.8", {"start": v(-80, -80) * mm, "mid": v(-77.07, -87.07) * mm, "end": v(-70, -90) * mm});
            skCircle(sketch, "E79.9", {"center": v(-60, -67.5) * mm, "radius": 4 * mm});
            skLineSegment(sketch, "E79.10", {"start": v(-60, 40.3) * mm, "end": v(-60, -40.3) * mm});
            skArc(sketch, "E79.11", {"start": v(-60, -40.3) * mm, "mid": v(-58.99, -44.68) * mm, "end": v(-56.15, -48.18) * mm});
            skArc(sketch, "E79.12", {"start": v(-56.15, -48.18) * mm, "mid": v(0, -67.5) * mm, "end": v(56.15, -48.18) * mm});
            skArc(sketch, "E79.13", {"start": v(56.15, -48.18) * mm, "mid": v(58.99, -44.68) * mm, "end": v(60, -40.3) * mm});
            skLineSegment(sketch, "E79.14", {"start": v(60, 40.3) * mm, "end": v(60, -40.3) * mm});
            skArc(sketch, "E79.15", {"start": v(56.15, 48.18) * mm, "mid": v(0, 67.5) * mm, "end": v(-56.15, 48.18) * mm});
            skArc(sketch, "E79.16", {"start": v(60, 40.3) * mm, "mid": v(58.99, 44.68) * mm, "end": v(56.15, 48.18) * mm});
            skArc(sketch, "E79.17", {"start": v(-56.15, 48.18) * mm, "mid": v(-58.99, 44.68) * mm, "end": v(-60, 40.3) * mm});
            skCircle(sketch, "E79.18", {"center": v(-60, 67.5) * mm, "radius": 4 * mm});
            skCircle(sketch, "E79.19", {"center": v(60, 67.5) * mm, "radius": 4 * mm});
            skCircle(sketch, "E79.20", {"center": v(60, -67.5) * mm, "radius": 4 * mm});
            skLineSegment(sketch, "E80", {"start": v(0, 23.75) * mm, "end": v(0, 120) * mm, "construction": true});
            skCircle(sketch, "E81", {"center": v(0, 120) * mm, "radius": 6 * mm});
            skLineSegment(sketch, "E82", {"start": v(-33, 90) * mm, "end": v(-15, 108) * mm});
            skLineSegment(sketch, "E83", {"start": v(-15, 108) * mm, "end": v(-15, 120) * mm});
            skLineSegment(sketch, "E84", {"start": v(15, 108) * mm, "end": v(15, 120) * mm});
            skArc(sketch, "E85", {"start": v(15, 120) * mm, "mid": v(0, 135) * mm, "end": v(-15, 120) * mm});
            skLineSegment(sketch, "E86", {"start": v(15, 108) * mm, "end": v(33, 90) * mm});
            skLineSegment(sketch, "E87", {"start": v(-80, 0) * mm, "end": v(80, 0) * mm, "construction": true});
            skLineSegment(sketch, "E88.MirrorCS", {"start": v(15, -108) * mm, "end": v(33, -90) * mm});
            skLineSegment(sketch, "E89.MirrorCS", {"start": v(15, -108) * mm, "end": v(15, -120) * mm});
            skArc(sketch, "E90.MirrorCS", {"start": v(15, -120) * mm, "mid": v(0, -135) * mm, "end": v(-15, -120) * mm});
            skLineSegment(sketch, "E91.MirrorCS", {"start": v(-15, -108) * mm, "end": v(-15, -120) * mm});
            skLineSegment(sketch, "E92.MirrorCS", {"start": v(-33, -90) * mm, "end": v(-15, -108) * mm});
            skCircle(sketch, "E93.MirrorC", {"center": v(0, -120) * mm, "radius": 6 * mm});
            skLineSegment(sketch, "E94.MirrorCS", {"start": v(0, -23.75) * mm, "end": v(0, -120) * mm, "construction": true});
            skSolve(sketch);
        }
        {
            var Q0;
            Q0 = qSketchRegion(id + "F16", true);
            var Q1;
            Q1=makeQuery(id+"F2.opExtrude","CAP_FACE",FACE,{"disambiguationData":[OSD([sQuery(id+"F0.wireOp",EDGE,"E12"),sQuery(id+"F0.wireOp",EDGE,"E13"),sQuery(id+"F0.wireOp",EDGE,"E14"),sQuery(id+"F0.wireOp",EDGE,"E15"),sQuery(id+"F0.wireOp",EDGE,"E17.filletArc"),sQuery(id+"F0.wireOp",EDGE,"E18.filletArc"),sQuery(id+"F0.wireOp",EDGE,"E19.filletArc"),sQuery(id+"F0.wireOp",EDGE,"E20.filletArc"),sQuery(id+"F0.wireOp",EDGE,"E25.0"),sQuery(id+"F0.wireOp",EDGE,"E25.1"),sQuery(id+"F0.wireOp",EDGE,"E25.2"),sQuery(id+"F0.wireOp",EDGE,"E25.3"),sQuery(id+"F0.wireOp",EDGE,"E25.4"),sQuery(id+"F0.wireOp",EDGE,"E25.5"),sQuery(id+"F0.wireOp",EDGE,"E25.6"),sQuery(id+"F0.wireOp",EDGE,"E25.7")])],"isStart":false});
            extrude(context, id + "F17", {"entities" : qUnion([Q0]), "endBound" : BoundingType.UP_TO_SURFACE, "depth" : 25 * mm, "endBoundEntityFace" : qUnion([Q1]), "offsetDistance" : 25 * mm});
        }
    });
